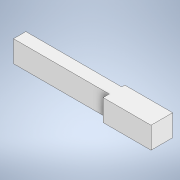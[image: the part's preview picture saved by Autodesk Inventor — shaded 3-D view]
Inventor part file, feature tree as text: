
AUTODESK INVENTOR PART (.ipt)
format: ipt  version: 2021 (Build 250183000, 183)  size: 99,840 bytes
history: native  units: in
note: dims shown in document units (in); Inventor stores cm internally (conversion verified against a paired STEP export)
features: extrude x1, sketch x1
ambient origin geometry x8: Origin, YZ Plane, XZ Plane, XY Plane, X Axis, Y Axis, Z Axis, Center Point
bodies: Solid1 (feature_tree)
feature tree (2):
  extrude  "Extrusion1"  Depth=5.8125in
  sketch  "Sketch1"  dims[d0=0.875in d1=5.8125in d2=3.875in d4=0.75in d5=0.625in d6=0.875in d7=0.0in]
